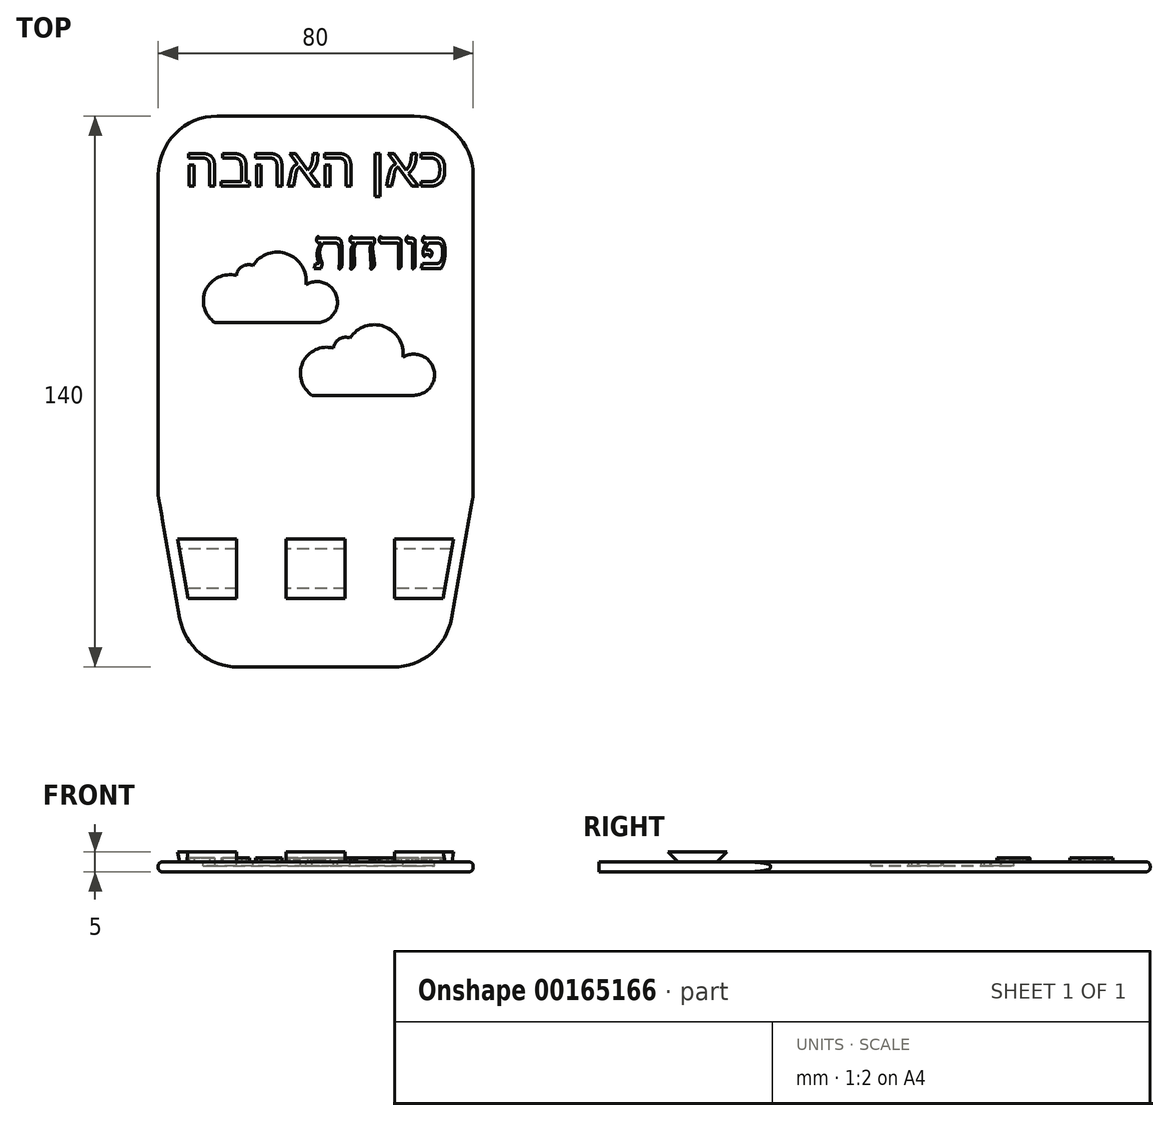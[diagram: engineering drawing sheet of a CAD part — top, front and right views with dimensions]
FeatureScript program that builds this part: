
annotation { "Feature Type Name" : "Feature", "Feature Type Description" : "" }
export const myFeature = defineFeature(function(context is Context, id is Id, definition is map)
    precondition{}
    {
        {
            var Q0;
            Q0=qCreatedBy(makeId("Right.planeOp"),FACE);
            var sketch = newSketch(context, id + "F0", { "sketchPlane" : qUnion([Q0])});
            skLineSegment(sketch, "E0.bottom", {"start": v(-70, 1.25) * mm, "end": v(-50, 1.25) * mm});
            skLineSegment(sketch, "E0.top", {"start": v(-70, -1.25) * mm, "end": v(70, -1.25) * mm});
            skLineSegment(sketch, "E0.left", {"start": v(-70, 1.25) * mm, "end": v(-70, -1.25) * mm});
            skLineSegment(sketch, "E0.right", {"start": v(70, 1.25) * mm, "end": v(70, -1.25) * mm});
            skLineSegment(sketch, "E1.top", {"start": v(-52.5, 3.75) * mm, "end": v(-37.5, 3.75) * mm});
            skLineSegment(sketch, "E2", {"start": v(-52.5, 3.75) * mm, "end": v(-50, 1.25) * mm});
            skLineSegment(sketch, "E3.trimOffspring", {"start": v(-40, 1.25) * mm, "end": v(70, 1.25) * mm});
            skLineSegment(sketch, "E4", {"start": v(-45, 3.75) * mm, "end": v(-45, -1.25) * mm, "construction": true});
            skLineSegment(sketch, "E5.MirrorCS", {"start": v(-37.5, 3.75) * mm, "end": v(-40, 1.25) * mm});
            skLineSegment(sketch, "E6", {"start": v(-70, 1.25) * mm, "end": v(70, -1.25) * mm, "construction": true});
            skSolve(sketch);
        }
        {
            var Q0;
            Q0 = qSketchRegion(id + "F0", true);
            extrude(context, id + "F1", {"entities" : qUnion([Q0]), "depth" : 80 * mm});
        }
        {
            var Q0;
            Q0=makeQuery(id+"F5.boolean.opBoolean","MERGE",FACE,{"derivedFrom":[makeQuery(id+"F1.opExtrude","SWEPT_FACE",FACE,{"disambiguationData":[OSD([sQuery(id+"F0.wireOp",EDGE,"E0.bottom")])]}),makeQuery(id+"F1.opExtrude","SWEPT_FACE",FACE,{"disambiguationData":[OSD([sQuery(id+"F0.wireOp",EDGE,"E3.trimOffspring")])]}),makeQuery(id+"F5.opExtrude","CAP_FACE",FACE,{"disambiguationData":[OSD([sQuery(id+"F4.wireOp",EDGE,"E16.bottom"),sQuery(id+"F4.wireOp",EDGE,"E16.top"),sQuery(id+"F4.wireOp",EDGE,"E16.left"),sQuery(id+"F4.wireOp",EDGE,"E16.right")])],"isStart":false}),makeQuery(id+"F5.opExtrude","CAP_FACE",FACE,{"disambiguationData":[OSD([sQuery(id+"F4.wireOp",EDGE,"E17.bottom"),sQuery(id+"F4.wireOp",EDGE,"E17.top"),sQuery(id+"F4.wireOp",EDGE,"E17.left"),sQuery(id+"F4.wireOp",EDGE,"E17.right")])],"isStart":false}),makeQuery(id+"F5.opExtrude","CAP_FACE",FACE,{"disambiguationData":[OSD([sQuery(id+"F4.wireOp",EDGE,"E18.bottom"),sQuery(id+"F4.wireOp",EDGE,"E18.top"),sQuery(id+"F4.wireOp",EDGE,"E18.left"),sQuery(id+"F4.wireOp",EDGE,"E18.right")])],"isStart":false}),makeQuery(id+"F5.opExtrude","CAP_FACE",FACE,{"disambiguationData":[OSD([sQuery(id+"F4.wireOp",EDGE,"E19.bottom"),sQuery(id+"F4.wireOp",EDGE,"E19.top"),sQuery(id+"F4.wireOp",EDGE,"E19.left"),sQuery(id+"F4.wireOp",EDGE,"E19.right")])],"isStart":false})]});
            var sketch = newSketch(context, id + "F2", { "sketchPlane" : qUnion([Q0])});
            skLineSegment(sketch, "E7", {"start": v(-9.78, -94.76) * mm, "end": v(89.78, -94.76) * mm});
            skLineSegment(sketch, "E8", {"start": v(89.78, -94.76) * mm, "end": v(89.78, -26.5) * mm});
            skLineSegment(sketch, "E9", {"start": v(89.78, -26.5) * mm, "end": v(80, -26.5) * mm});
            skLineSegment(sketch, "E10", {"start": v(80, -26.5) * mm, "end": v(71.2, -76.43) * mm});
            skLineSegment(sketch, "E11", {"start": v(71.2, -76.43) * mm, "end": v(8.8, -76.43) * mm});
            skLineSegment(sketch, "E12", {"start": v(40, -94.76) * mm, "end": v(40, -69.14) * mm, "construction": true});
            skLineSegment(sketch, "E13.MirrorCS", {"start": v(0, -26.5) * mm, "end": v(8.8, -76.43) * mm});
            skLineSegment(sketch, "E14.MirrorCS", {"start": v(-9.78, -26.5) * mm, "end": v(0, -26.5) * mm});
            skLineSegment(sketch, "E15.MirrorCS", {"start": v(-9.78, -94.76) * mm, "end": v(-9.78, -26.5) * mm});
            skSolve(sketch);
        }
        {
            var Q0;
            Q0 = qSketchRegion(id + "F2", true);
            extrude(context, id + "F3", {"entities" : qUnion([Q0]), "operationType" : NewBodyOperationType.REMOVE, "endBound" : BoundingType.SYMMETRIC, "oppositeDirection" : true, "depth" : 25 * mm});
        }
        {
            var Q0;
            Q0=makeQuery(id+"F1.opExtrude","SWEPT_FACE",FACE,{"disambiguationData":[OSD([sQuery(id+"F0.wireOp",EDGE,"E1.top")])]});
            var sketch = newSketch(context, id + "F4", { "sketchPlane" : qUnion([Q0])});
            skLineSegment(sketch, "E16.bottom", {"start": v(1.94, -37.5) * mm, "end": v(4.94, -37.5) * mm});
            skLineSegment(sketch, "E16.top", {"start": v(4.58, -52.5) * mm, "end": v(7.58, -52.5) * mm});
            skLineSegment(sketch, "E16.left", {"start": v(1.94, -37.5) * mm, "end": v(4.58, -52.5) * mm});
            skLineSegment(sketch, "E16.right", {"start": v(4.94, -37.5) * mm, "end": v(7.58, -52.5) * mm});
            skLineSegment(sketch, "E17.bottom", {"start": v(78.06, -37.5) * mm, "end": v(75.06, -37.5) * mm});
            skLineSegment(sketch, "E17.top", {"start": v(75.42, -52.5) * mm, "end": v(72.42, -52.5) * mm});
            skLineSegment(sketch, "E17.left", {"start": v(78.06, -37.5) * mm, "end": v(75.42, -52.5) * mm});
            skLineSegment(sketch, "E17.right", {"start": v(75.06, -37.5) * mm, "end": v(72.42, -52.5) * mm});
            skLineSegment(sketch, "E18.bottom", {"start": v(19.94, -37.5) * mm, "end": v(32.5, -37.5) * mm});
            skLineSegment(sketch, "E18.top", {"start": v(19.94, -52.5) * mm, "end": v(32.5, -52.5) * mm});
            skLineSegment(sketch, "E18.left", {"start": v(19.94, -37.5) * mm, "end": v(19.94, -52.5) * mm});
            skLineSegment(sketch, "E18.right", {"start": v(32.5, -37.5) * mm, "end": v(32.5, -52.5) * mm});
            skLineSegment(sketch, "E19.bottom", {"start": v(47.5, -37.5) * mm, "end": v(60.06, -37.5) * mm});
            skLineSegment(sketch, "E19.top", {"start": v(47.5, -52.5) * mm, "end": v(60.06, -52.5) * mm});
            skLineSegment(sketch, "E19.left", {"start": v(47.5, -37.5) * mm, "end": v(47.5, -52.5) * mm});
            skLineSegment(sketch, "E19.right", {"start": v(60.06, -37.5) * mm, "end": v(60.06, -52.5) * mm});
            skLineSegment(sketch, "E20", {"start": v(4.94, -37.5) * mm, "end": v(19.94, -37.5) * mm, "construction": true});
            skLineSegment(sketch, "E21", {"start": v(32.5, -37.5) * mm, "end": v(47.5, -37.5) * mm, "construction": true});
            skLineSegment(sketch, "E22", {"start": v(60.06, -37.5) * mm, "end": v(75.06, -37.5) * mm, "construction": true});
            skSolve(sketch);
        }
        {
            var Q0;
            Q0 = qSketchRegion(id + "F4", true);
            extrude(context, id + "F5", {"entities" : qUnion([Q0]), "operationType" : NewBodyOperationType.REMOVE, "oppositeDirection" : true, "depth" : 2.5 * mm});
        }
        {
            var Q0;
            Q0=makeQuery(id+"F1.opExtrude","CAP_EDGE",EDGE,{"disambiguationData":[OSD([sQuery(id+"F0.wireOp",EDGE,"E0.right")])],"isStart":false});
            var Q1;
            Q1=makeQuery(id+"F1.opExtrude","CAP_EDGE",EDGE,{"disambiguationData":[OSD([sQuery(id+"F0.wireOp",EDGE,"E0.right")])],"isStart":true});
            var Q2;
            Q2=makeQuery(id+"F3.boolean.opBoolean","INTERSECT",EDGE,{"derivedFrom":[makeQuery(id+"F1.opExtrude","SWEPT_FACE",FACE,{"disambiguationData":[OSD([sQuery(id+"F0.wireOp",EDGE,"E0.left")])]}),makeQuery(id+"F3.opExtrude","SWEPT_FACE",FACE,{"disambiguationData":[OSD([sQuery(id+"F2.wireOp",EDGE,"E13.MirrorCS")])]})]});
            var Q3;
            Q3=makeQuery(id+"F3.boolean.opBoolean","INTERSECT",EDGE,{"derivedFrom":[makeQuery(id+"F1.opExtrude","SWEPT_FACE",FACE,{"disambiguationData":[OSD([sQuery(id+"F0.wireOp",EDGE,"E0.left")])]}),makeQuery(id+"F3.opExtrude","SWEPT_FACE",FACE,{"disambiguationData":[OSD([sQuery(id+"F2.wireOp",EDGE,"E10")])]})]});
            var Q4;
            Q4=makeQuery(id+"F3.boolean.opBoolean","COPY",EDGE,{"derivedFrom":makeQuery(id+"F3.opExtrude","SWEPT_EDGE",EDGE,{"disambiguationData":[OSD([sQuery(id+"F0.wireOp",EDGE,"E3.trimOffspring"),sQuery(id+"F2.wireOp",EDGE,"E13.MirrorCS"),sQuery(id+"F2.wireOp",EDGE,"E14.MirrorCS")])]})});
            var Q5;
            Q5=makeQuery(id+"F3.boolean.opBoolean","COPY",EDGE,{"derivedFrom":makeQuery(id+"F3.opExtrude","SWEPT_EDGE",EDGE,{"disambiguationData":[OSD([sQuery(id+"F0.wireOp",EDGE,"E3.trimOffspring"),sQuery(id+"F2.wireOp",EDGE,"E9"),sQuery(id+"F2.wireOp",EDGE,"E10")])]})});
            fillet(context, id + "F6", {"entities" : qUnion([Q0, Q1, Q2, Q3, Q4, Q5]), "radius" : 15 * mm, "tangentPropagation" : true, "allowEdgeOverflow" : false});
        }
        {
            var Q0;
            Q0=makeQuery(id+"F5.boolean.opBoolean","MERGE",FACE,{"derivedFrom":[makeQuery(id+"F1.opExtrude","SWEPT_FACE",FACE,{"disambiguationData":[OSD([sQuery(id+"F0.wireOp",EDGE,"E0.bottom")])]}),makeQuery(id+"F1.opExtrude","SWEPT_FACE",FACE,{"disambiguationData":[OSD([sQuery(id+"F0.wireOp",EDGE,"E3.trimOffspring")])]}),makeQuery(id+"F5.opExtrude","CAP_FACE",FACE,{"disambiguationData":[OSD([sQuery(id+"F4.wireOp",EDGE,"E16.bottom"),sQuery(id+"F4.wireOp",EDGE,"E16.top"),sQuery(id+"F4.wireOp",EDGE,"E16.left"),sQuery(id+"F4.wireOp",EDGE,"E16.right")])],"isStart":false})]});
            var sketch = newSketch(context, id + "F7", { "sketchPlane" : qUnion([Q0])});
            skLineSegment(sketch, "E23", {"start": v(39.11, -0.93) * mm, "end": v(64.97, -0.93) * mm});
            skArc(sketch, "E24", {"start": v(44.52, 11.03) * mm, "mid": v(36.71, 7.36) * mm, "end": v(39.11, -0.93) * mm});
            skArc(sketch, "E25", {"start": v(48.73, 13.62) * mm, "mid": v(46, 13.35) * mm, "end": v(44.52, 11.03) * mm});
            skArc(sketch, "E26", {"start": v(62.2, 8.72) * mm, "mid": v(57.42, 16.55) * mm, "end": v(48.73, 13.62) * mm});
            skArc(sketch, "E27", {"start": v(64.97, -0.93) * mm, "mid": v(70, 5.74) * mm, "end": v(62.2, 8.72) * mm});
            skLineSegment(sketch, "E28", {"start": v(14.45, 17.5) * mm, "end": v(40.31, 17.5) * mm});
            skArc(sketch, "E29", {"start": v(19.86, 29.47) * mm, "mid": v(12.05, 25.8) * mm, "end": v(14.45, 17.5) * mm});
            skArc(sketch, "E30", {"start": v(24.07, 32.05) * mm, "mid": v(21.33, 31.79) * mm, "end": v(19.86, 29.47) * mm});
            skArc(sketch, "E31", {"start": v(37.54, 27.16) * mm, "mid": v(32.76, 34.99) * mm, "end": v(24.07, 32.05) * mm});
            skArc(sketch, "E32", {"start": v(40.31, 17.5) * mm, "mid": v(45.33, 24.17) * mm, "end": v(37.54, 27.16) * mm});
            skSolve(sketch);
        }
        {
            var Q0;
            Q0 = qSketchRegion(id + "F7", true);
            extrude(context, id + "F8", {"entities" : qUnion([Q0]), "operationType" : NewBodyOperationType.REMOVE, "oppositeDirection" : true, "depth" : 1 * mm});
        }
        {
            var Q0;
            Q0=makeQuery(id+"F5.boolean.opBoolean","MERGE",EDGE,{"derivedFrom":[makeQuery(id+"F1.opExtrude","CAP_EDGE",EDGE,{"disambiguationData":[OSD([sQuery(id+"F0.wireOp",EDGE,"E0.bottom")])],"isStart":true}),makeQuery(id+"F1.opExtrude","CAP_EDGE",EDGE,{"disambiguationData":[OSD([sQuery(id+"F0.wireOp",EDGE,"E3.trimOffspring")])],"isStart":true}),makeQuery(id+"F5.opExtrude","CAP_EDGE",EDGE,{"disambiguationData":[OSD([sQuery(id+"F4.wireOp",EDGE,"E16.left")])],"isStart":false})]});
            var Q1;
            Q1=makeQuery(id+"F1.opExtrude","CAP_EDGE",EDGE,{"disambiguationData":[OSD([sQuery(id+"F0.wireOp",EDGE,"E0.top")])],"isStart":true});
            var Q2;
            Q2=makeQuery(id+"F8.boolean.opBoolean","COPY",EDGE,{"derivedFrom":makeQuery(id+"F8.opExtrude","CAP_EDGE",EDGE,{"disambiguationData":[OSD([sQuery(id+"F7.wireOp",EDGE,"E27")])],"isStart":true})});
            var Q3;
            Q3=makeQuery(id+"F8.boolean.opBoolean","COPY",EDGE,{"derivedFrom":makeQuery(id+"F8.opExtrude","CAP_EDGE",EDGE,{"disambiguationData":[OSD([sQuery(id+"F7.wireOp",EDGE,"E26")])],"isStart":true})});
            var Q4;
            Q4=makeQuery(id+"F8.boolean.opBoolean","COPY",EDGE,{"derivedFrom":makeQuery(id+"F8.opExtrude","CAP_EDGE",EDGE,{"disambiguationData":[OSD([sQuery(id+"F7.wireOp",EDGE,"E25")])],"isStart":true})});
            var Q5;
            Q5=makeQuery(id+"F8.boolean.opBoolean","COPY",EDGE,{"derivedFrom":makeQuery(id+"F8.opExtrude","CAP_EDGE",EDGE,{"disambiguationData":[OSD([sQuery(id+"F7.wireOp",EDGE,"E24")])],"isStart":true})});
            var Q6;
            Q6=makeQuery(id+"F8.boolean.opBoolean","COPY",EDGE,{"derivedFrom":makeQuery(id+"F8.opExtrude","CAP_EDGE",EDGE,{"disambiguationData":[OSD([sQuery(id+"F7.wireOp",EDGE,"E32")])],"isStart":true})});
            var Q7;
            Q7=makeQuery(id+"F8.boolean.opBoolean","COPY",EDGE,{"derivedFrom":makeQuery(id+"F8.opExtrude","CAP_EDGE",EDGE,{"disambiguationData":[OSD([sQuery(id+"F7.wireOp",EDGE,"E31")])],"isStart":true})});
            var Q8;
            Q8=makeQuery(id+"F8.boolean.opBoolean","COPY",EDGE,{"derivedFrom":makeQuery(id+"F8.opExtrude","CAP_EDGE",EDGE,{"disambiguationData":[OSD([sQuery(id+"F7.wireOp",EDGE,"E29")])],"isStart":true})});
            var Q9;
            Q9=makeQuery(id+"F8.boolean.opBoolean","COPY",EDGE,{"derivedFrom":makeQuery(id+"F8.opExtrude","CAP_EDGE",EDGE,{"disambiguationData":[OSD([sQuery(id+"F7.wireOp",EDGE,"E30")])],"isStart":true})});
            fillet(context, id + "F9", {"entities" : qUnion([Q0, Q1, Q2, Q3, Q4, Q5, Q6, Q7, Q8, Q9]), "radius" : 1 * mm, "tangentPropagation" : true, "allowEdgeOverflow" : false});
        }
        {
            var Q0;
            Q0=makeQuery(id+"F5.boolean.opBoolean","MERGE",FACE,{"derivedFrom":[makeQuery(id+"F1.opExtrude","SWEPT_FACE",FACE,{"disambiguationData":[OSD([sQuery(id+"F0.wireOp",EDGE,"E0.bottom")])]}),makeQuery(id+"F1.opExtrude","SWEPT_FACE",FACE,{"disambiguationData":[OSD([sQuery(id+"F0.wireOp",EDGE,"E3.trimOffspring")])]}),makeQuery(id+"F5.opExtrude","CAP_FACE",FACE,{"disambiguationData":[OSD([sQuery(id+"F4.wireOp",EDGE,"E16.bottom"),sQuery(id+"F4.wireOp",EDGE,"E16.top"),sQuery(id+"F4.wireOp",EDGE,"E16.left"),sQuery(id+"F4.wireOp",EDGE,"E16.right")])],"isStart":false})]});
            var sketch = newSketch(context, id + "F10", { "sketchPlane" : qUnion([Q0])});
            skText(sketch, "E33", { "text": "הבהאה ןאכ", "fontName": "Arimo-Regular.ttf"});
            skText(sketch, "E34", { "text": "תחרופ", "fontName": "Tinos-Regular.ttf"});
            const initialGuessF10  = {"E33": [0.00665, 0.0522, 1, 0, 0.01], "E34": [0.03929, 0.03128, 1, 0, 0.01]};
            skSetInitialGuess(sketch, initialGuessF10);
            skSolve(sketch);
        }
        {
            var Q0;
            Q0 = qSketchRegion(id + "F10", true);
            extrude(context, id + "F11", {"entities" : qUnion([Q0]), "operationType" : NewBodyOperationType.ADD, "depth" : 1 * mm});
        }
    });
